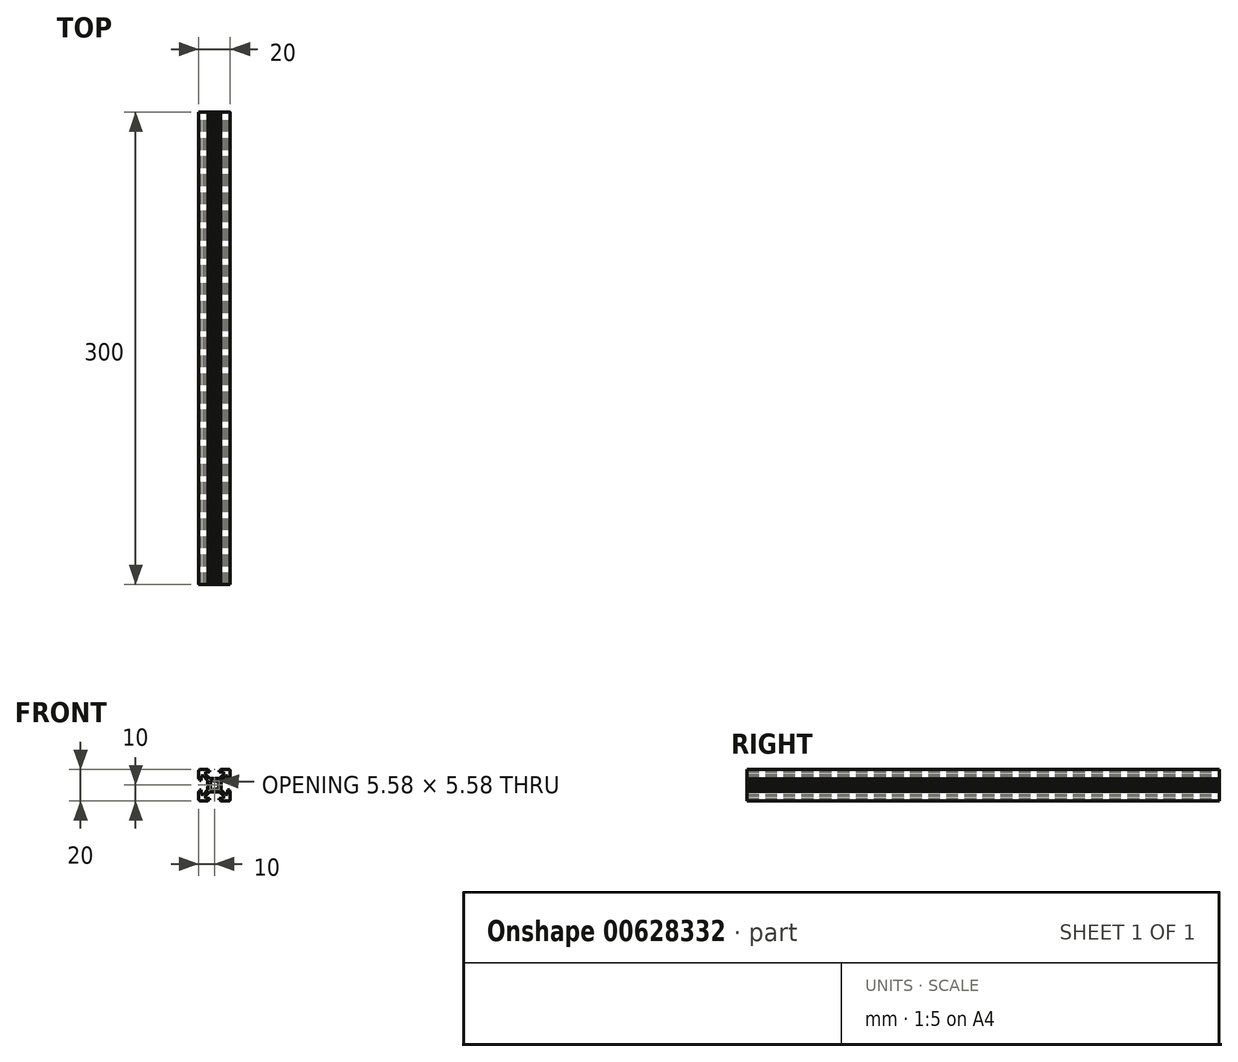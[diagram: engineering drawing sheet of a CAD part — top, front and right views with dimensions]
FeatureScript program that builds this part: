
annotation { "Feature Type Name" : "Feature", "Feature Type Description" : "" }
export const myFeature = defineFeature(function(context is Context, id is Id, definition is map)
    precondition{}
    {
        {
            var Q0;
            Q0=qCreatedBy(makeId("Front.planeOp"),FACE);
            var sketch = newSketch(context, id + "F0", { "sketchPlane" : qUnion([Q0])});
            skArc(sketch, "E0", {"start": v(-2.43, 1.3) * mm, "mid": v(-2.67, 0.67) * mm, "end": v(-2.75, 0) * mm});
            skPoint(sketch, "E1.visualSharp", {"position": v(-10, 10) * mm});
            skArc(sketch, "E1.filletArc", {"start": v(-9, 10) * mm, "mid": v(-9.7, 9.7) * mm, "end": v(-10, 9) * mm});
            skLineSegment(sketch, "E2", {"start": v(-3.85, 0) * mm, "end": v(0, 0) * mm, "construction": true});
            skLineSegment(sketch, "E3", {"start": v(0, 3.85) * mm, "end": v(0, 0) * mm, "construction": true});
            skLineSegment(sketch, "E4.0", {"start": v(-9.5, 3) * mm, "end": v(-8.4, 3) * mm});
            skLineSegment(sketch, "E5.0", {"start": v(-3, 9.5) * mm, "end": v(-3, 8.4) * mm});
            skLineSegment(sketch, "E6.trimOffspring", {"start": v(-10, 4) * mm, "end": v(-10, 9) * mm});
            skLineSegment(sketch, "E7.trimOffspring", {"start": v(-4, 10) * mm, "end": v(-9, 10) * mm});
            skLineSegment(sketch, "E8.0", {"start": v(-3, 8.4) * mm, "end": v(-5.8, 8.4) * mm});
            skLineSegment(sketch, "E8.1", {"start": v(-8.4, 3) * mm, "end": v(-8.4, 5.8) * mm});
            skLineSegment(sketch, "E9", {"start": v(-8.4, 8.4) * mm, "end": v(0, 0) * mm, "construction": true});
            skLineSegment(sketch, "E10.0", {"start": v(-5.8, 6.93) * mm, "end": v(-3.12, 4.25) * mm});
            skLineSegment(sketch, "E11.0", {"start": v(-6.93, 5.8) * mm, "end": v(-4.25, 3.12) * mm});
            skArc(sketch, "E12.trimOffspring", {"start": v(-1.66, 2.79) * mm, "mid": v(-2.3, 2.3) * mm, "end": v(-2.79, 1.66) * mm});
            skLineSegment(sketch, "E13.top", {"start": v(-10, 4) * mm, "end": v(-9.5, 4) * mm});
            skLineSegment(sketch, "E13.right", {"start": v(-9.5, 3) * mm, "end": v(-9.5, 4) * mm});
            skLineSegment(sketch, "E14.top", {"start": v(-3, 9.5) * mm, "end": v(-4, 9.5) * mm});
            skLineSegment(sketch, "E14.right", {"start": v(-4, 10) * mm, "end": v(-4, 9.5) * mm});
            skLineSegment(sketch, "E15.bottom", {"start": v(-3.12, 4.25) * mm, "end": v(-0.75, 4.25) * mm});
            skLineSegment(sketch, "E15.left", {"start": v(-4.25, 3.12) * mm, "end": v(-4.25, 0.75) * mm});
            skLineSegment(sketch, "E16", {"start": v(-8.4, 5.8) * mm, "end": v(-6.93, 5.8) * mm});
            skLineSegment(sketch, "E17", {"start": v(-5.8, 8.4) * mm, "end": v(-5.8, 6.93) * mm});
            skPoint(sketch, "E18.orphan", {"position": v(-4.25, 4.25) * mm});
            skLineSegment(sketch, "E19.trimOffspring", {"start": v(-2.79, 1.66) * mm, "end": v(-2.43, 1.3) * mm});
            skLineSegment(sketch, "E20.trimOffspring", {"start": v(-1.66, 2.79) * mm, "end": v(-1.3, 2.43) * mm});
            skLineSegment(sketch, "E21", {"start": v(-4.25, 0.75) * mm, "end": v(-3.85, 0) * mm});
            skPoint(sketch, "E22.orphan", {"position": v(-4.25, 0) * mm});
            skLineSegment(sketch, "E23", {"start": v(0, 3.85) * mm, "end": v(-0.75, 4.25) * mm});
            skPoint(sketch, "E24.orphan", {"position": v(0, 4.25) * mm});
            skArc(sketch, "E25.trimOffspring", {"start": v(0, 2.75) * mm, "mid": v(-0.67, 2.67) * mm, "end": v(-1.3, 2.43) * mm});
            skLineSegment(sketch, "E26", {"start": v(0, 2.75) * mm, "end": v(0, 3.85) * mm});
            skLineSegment(sketch, "E27", {"start": v(-3.85, 0) * mm, "end": v(-2.75, 0) * mm});
            skSolve(sketch);
        }
        {
            var Q0;
            Q0=qSketchRegion(id+"F0",true);
            extrude(context, id + "F1", {"entities" : qUnion([Q0]), "depth" : 300 * mm});
        }
        {
            var Q0;
            Q0=qCreatedBy(makeId("Top.planeOp"),FACE);
            var sketch = newSketch(context, id + "F2", { "sketchPlane" : qUnion([Q0])});
            skLineSegment(sketch, "E28", {"start": v(0, 0) * mm, "end": v(0, -300) * mm, "construction": true});
            skSolve(sketch);
        }
        {
            var Q0;
            Q0=makeQuery(id+"F1.opExtrude","SWEPT_BODY",BODY,{"disambiguationData":[OSD([sQuery(id+"F0.wireOp",EDGE,"E0"),sQuery(id+"F0.wireOp",EDGE,"E1.filletArc"),sQuery(id+"F0.wireOp",EDGE,"E4.0"),sQuery(id+"F0.wireOp",EDGE,"E5.0"),sQuery(id+"F0.wireOp",EDGE,"E6.trimOffspring"),sQuery(id+"F0.wireOp",EDGE,"E7.trimOffspring"),sQuery(id+"F0.wireOp",EDGE,"E8.0"),sQuery(id+"F0.wireOp",EDGE,"E8.1"),sQuery(id+"F0.wireOp",EDGE,"E10.0"),sQuery(id+"F0.wireOp",EDGE,"E11.0"),sQuery(id+"F0.wireOp",EDGE,"E12.trimOffspring"),sQuery(id+"F0.wireOp",EDGE,"E13.top"),sQuery(id+"F0.wireOp",EDGE,"E13.right"),sQuery(id+"F0.wireOp",EDGE,"E14.top"),sQuery(id+"F0.wireOp",EDGE,"E14.right"),sQuery(id+"F0.wireOp",EDGE,"E15.bottom"),sQuery(id+"F0.wireOp",EDGE,"E15.left"),sQuery(id+"F0.wireOp",EDGE,"E16"),sQuery(id+"F0.wireOp",EDGE,"E17"),sQuery(id+"F0.wireOp",EDGE,"E19.trimOffspring"),sQuery(id+"F0.wireOp",EDGE,"E20.trimOffspring"),sQuery(id+"F0.wireOp",EDGE,"E21"),sQuery(id+"F0.wireOp",EDGE,"E23"),sQuery(id+"F0.wireOp",EDGE,"E25.trimOffspring"),sQuery(id+"F0.wireOp",EDGE,"E26"),sQuery(id+"F0.wireOp",EDGE,"E27")])]});
            var Q1;
            Q1=sQuery(id+"F2.wireOp",EDGE,"E28");
            circularPattern(context, id + "F3", {"operationType" : NewBodyOperationType.ADD, "entities" : qUnion([Q0]), "axis" : qUnion([Q1]), "angle" : 360 * degree, "instanceCount" : 4, "equalSpace" : true});
        }
    });
